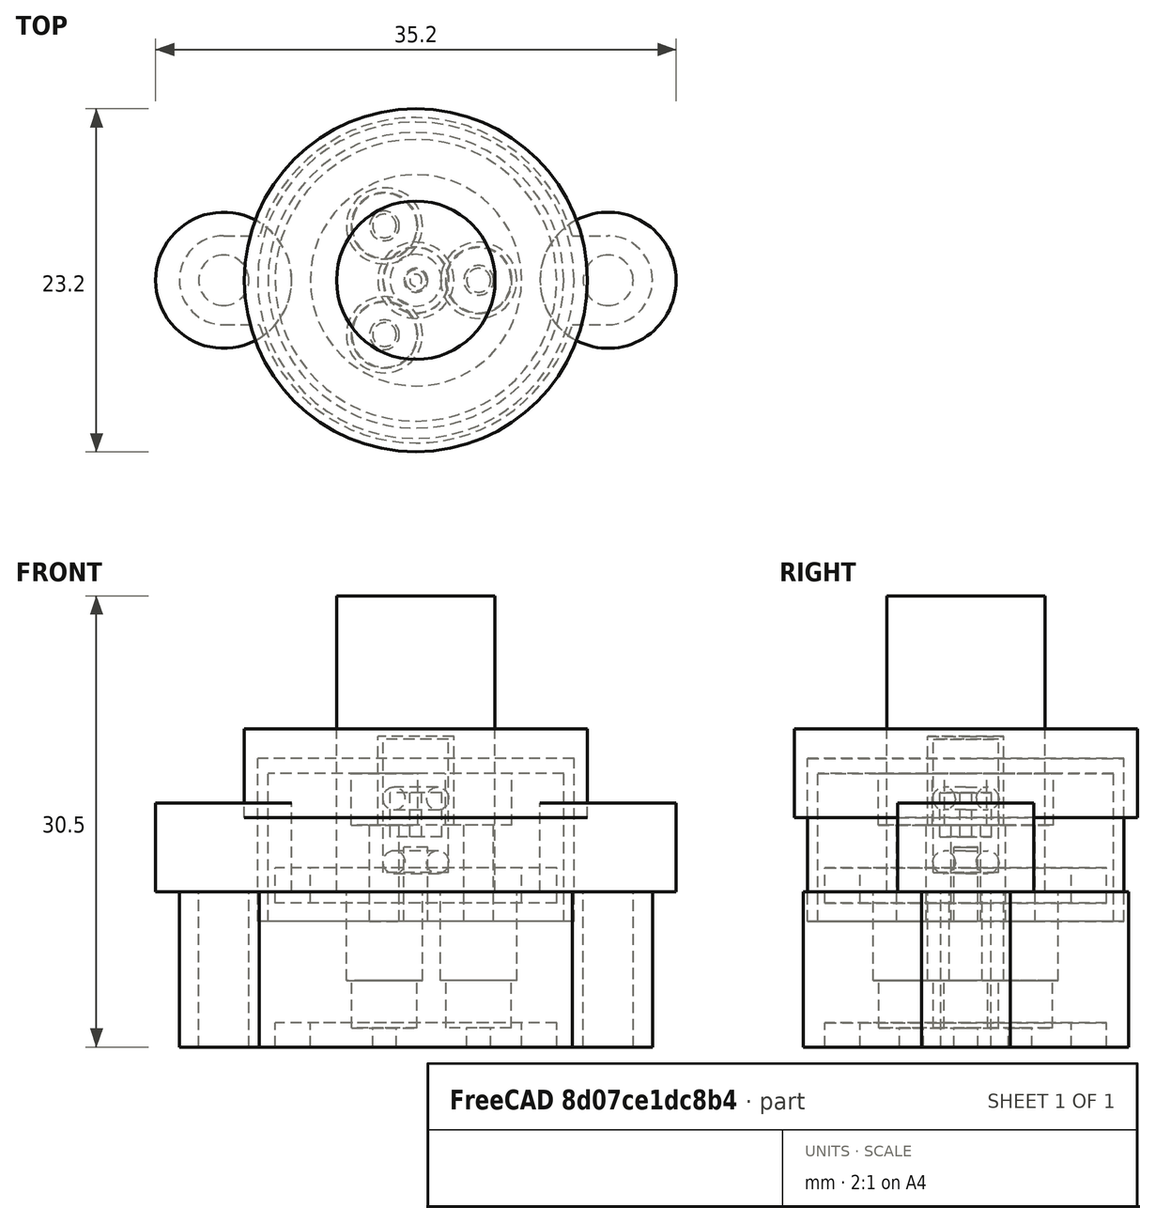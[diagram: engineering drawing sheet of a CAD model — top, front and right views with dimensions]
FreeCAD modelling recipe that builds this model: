
FCSTD DOCUMENT  (FreeCAD 0.17R13509 (Git))
Label: ceramic_wire_feedthroughs_insert_tail_negative
License: All rights reserved
LicenseURL: http://en.wikipedia.org/wiki/All_rights_reserved
objects: Part::Cylinder×46, Part::Cut×10, Part::MultiFuse×10, Part::Box×6, Part::FeaturePython×4, Part::Feature×2, App::FeaturePython×1
note: 78 computed .brp shape members not serialized (recipe doc carries the construction recipe); baked Part::Feature solids carry a one-line shape summary decoded from their .brp

FEATURE [Part::Cylinder] Cylinder155  label="Cylinder009"
  Angle = 360
  AttacherType = Attacher::AttachEngine3D
  Height = 2.38125
  Radius = 9.525
  expr: Radius = 3 / 4 * 25.399999999999999 / 2
  expr: Height = 3 / 32 * 25.399999999999999
FEATURE [Part::Cylinder] Cylinder154  label="Cylinder008"
  Angle = 360
  AttacherType = Attacher::AttachEngine3D
  Height = 2.38125
  Radius = 7.14375
  expr: Radius = 9 / 16 * 25.399999999999999 / 2
  expr: Height = 3 / 32 * 25.399999999999999
FEATURE [Part::Feature] Part__Feature001  label="TopOring"
  Placement = pos=(0,0,6.3) rot=(0,0,1;0rad)
  shape: bbox 4.839 x 4.839 x 1.524 mm, 4 faces (baked)
FEATURE [Part::Feature] Part__Feature002  label="BottomOring"
  Placement = pos=(0,0,2) rot=(0,0,1;0rad)
  shape: bbox 4.839 x 4.839 x 1.524 mm, 4 faces (baked)
FEATURE [Part::Cylinder] Cylinder153  label="Body"
  Angle = 360
  AttacherType = Attacher::AttachEngine3D
  Height = 10
  Placement = pos=(0,0,-2) rot=(0,0,1;0rad)
  Radius = 10
FEATURE [Part::Cut] Cut019  label="Oring"
  Base = -> Cylinder155
  Placement = pos=(0,0,-0.75) rot=(0,0,1;0rad)
  Tool = -> Cylinder154
FEATURE [Part::Cylinder] Cylinder147  label="ThreadedSection"
  Angle = 360
  AttacherType = Attacher::AttachEngine3D
  Height = 1
  Placement = pos=(0,0,4.5) rot=(0,0,1;0rad)
  Radius = 1
FEATURE [Part::Cylinder] Cylinder149  label="FTBead"
  Angle = 360
  AttacherType = Attacher::AttachEngine3D
  Height = 3
  Placement = pos=(0,0,2.7) rot=(0,0,1;0rad)
  Radius = 1.75
  expr: Radius = 3.5 / 2
FEATURE [Part::Cylinder] Cylinder152  label="RFFeeds005"
  Angle = 360
  AttacherType = Attacher::AttachEngine3D
  Height = 20
  Radius = 5.35813
  expr: Placement.Base.x = 0
FEATURE [Part::Cylinder] Cylinder156  label="BottomWireOutlet"
  Angle = 360
  AttacherType = Attacher::AttachEngine3D
  Height = 14
  Placement = pos=(0,0,-7) rot=(0,0,1;0rad)
  Radius = 1
FEATURE [Part::Cylinder] Cylinder157  label="SealSubtraction"
  Angle = 360
  AttacherType = Attacher::AttachEngine3D
  Height = 7
  Placement = pos=(0,0,4.5) rot=(0,0,1;0rad)
  Radius = 2.25
FEATURE [Part::MultiFuse] Fusion
  Placement = pos=(4.25,0,0) rot=(0,0,1;0rad)
  Shapes = -> [Cylinder147,Cylinder157,Cylinder156]
FEATURE [Part::FeaturePython] Array  label="SealArray"  # Draft array (typed FeaturePython)
  Angle = 360
  ArrayType = 1
  Axis = (0,0,1)
  Base = -> Fusion
  Center = (0,0,0)
  Fuse = false
  IntervalAxis = (0,0,0)
  IntervalX = (1,0,0)
  IntervalY = (0,1,0)
  IntervalZ = (0,0,0)
  NumberPolar = 3
  NumberX = 2
  NumberY = 2
  NumberZ = 1
FEATURE [Part::Cylinder] Cylinder159  label="FTBeadHole"
  Angle = 360
  AttacherType = Attacher::AttachEngine3D
  Height = 17
  Radius = 0.405
  expr: Radius = 0.81000000000000005 / 2
FEATURE [Part::Cut] Cut020
  Base = -> Cylinder149
  Placement = pos=(0,0,1) rot=(0,0,1;0rad)
  Tool = -> Cylinder159
FEATURE [Part::Cylinder] Cylinder160  label="Cylinder010"
  Angle = 360
  AttacherType = Attacher::AttachEngine3D
  Height = 2.38125
  Radius = 9.525
  expr: Radius = 3 / 4 * 25.399999999999999 / 2
  expr: Height = 3 / 32 * 25.399999999999999
FEATURE [Part::Cylinder] Cylinder161  label="WireFeedsMount003"
  Angle = 360
  AttacherType = Attacher::AttachEngine3D
  Height = 11
  Placement = pos=(-13,0,0) rot=(0,0,1;0rad)
  Radius = 1.7
FEATURE [Part::Cylinder] Cylinder162  label="ThreadedSection001"
  Angle = 360
  AttacherType = Attacher::AttachEngine3D
  Height = 6
  Placement = pos=(0,0,4.5) rot=(0,0,1;0rad)
  Radius = 2.575
  expr: Radius = 5.1500000000000004 / 2
FEATURE [Part::Cylinder] Cylinder163  label="Cylinder011"
  Angle = 360
  AttacherType = Attacher::AttachEngine3D
  Height = 2.38125
  Radius = 7.14375
  expr: Radius = 9 / 16 * 25.399999999999999 / 2
  expr: Height = 3 / 32 * 25.399999999999999
FEATURE [Part::Cut] Cut022  label="Oring001"
  Base = -> Cylinder160
  Placement = pos=(0,0,-0.75) rot=(0,0,1;0rad)
  Tool = -> Cylinder163
FEATURE [Part::Cylinder] Cylinder164  label="Body001"
  Angle = 360
  AttacherType = Attacher::AttachEngine3D
  Height = 10.5
  Radius = 11
FEATURE [Part::Cylinder] Cylinder165  label="WireFeedsMount004"
  Angle = 360
  AttacherType = Attacher::AttachEngine3D
  Height = 11
  Placement = pos=(13,0,0) rot=(0,0,1;0rad)
  Radius = 1.7
FEATURE [Part::Cylinder] Cylinder166  label="BottomWireOutlet001"
  Angle = 360
  AttacherType = Attacher::AttachEngine3D
  Height = 5
  Placement = pos=(0,0,-2) rot=(0,0,1;0rad)
  Radius = 0.8
FEATURE [Part::Cylinder] Cylinder167  label="SealSubtraction001"
  Angle = 360
  AttacherType = Attacher::AttachEngine3D
  Height = 9
  Placement = pos=(0,0,1.3) rot=(0,0,1;0rad)
  Radius = 2.2
FEATURE [Part::Box] Box002  label="MountCube003"
  AttacherType = Attacher::AttachEngine3D
  Height = 10.5
  Length = 3
  Placement = pos=(10,-3,0) rot=(0,0,1;0rad)
  Width = 6
FEATURE [Part::Box] Box003  label="MountCube004"
  AttacherType = Attacher::AttachEngine3D
  Height = 10.5
  Length = 3
  Placement = pos=(-13,-3,0) rot=(0,0,1;0rad)
  Width = 6
FEATURE [Part::MultiFuse] Fusion004
  Placement = pos=(4.25,0,0) rot=(0,0,1;0rad)
  Shapes = -> [Cylinder162,Cylinder167,Cylinder166]
FEATURE [Part::Cylinder] Cylinder168  label="MountFlange003"
  Angle = 360
  AttacherType = Attacher::AttachEngine3D
  Height = 10.5
  Placement = pos=(-13,0,0) rot=(0,0,1;0rad)
  Radius = 3
FEATURE [Part::Cylinder] Cylinder169  label="MountFlange004"
  Angle = 360
  AttacherType = Attacher::AttachEngine3D
  Height = 10.5
  Placement = pos=(13,0,0) rot=(0,0,1;0rad)
  Radius = 3
FEATURE [Part::MultiFuse] Fusion003
  Shapes = -> [Cylinder169,Box002,Box003,Cylinder168,Cylinder164]
FEATURE [Part::FeaturePython] Array001  label="SealArray001"  # Draft array (typed FeaturePython)
  Angle = 360
  ArrayType = 1
  Axis = (0,0,1)
  Base = -> Fusion004
  Center = (0,0,0)
  Fuse = false
  IntervalAxis = (0,0,0)
  IntervalX = (1,0,0)
  IntervalY = (0,1,0)
  IntervalZ = (0,0,0)
  NumberPolar = 3
  NumberX = 2
  NumberY = 2
  NumberZ = 1
FEATURE [Part::MultiFuse] Fusion005
  Shapes = -> [Cylinder165,Cylinder161,Cut022,Array001]
FEATURE [Part::Cut] Cut021
  Base = -> Fusion003
  Placement = pos=(0,0,-10.5) rot=(0,0,1;0rad)
  Tool = -> Fusion005
FEATURE [Part::Cylinder] Cylinder170  label="Cylinder012"
  Angle = 360
  AttacherType = Attacher::AttachEngine3D
  Height = 2.38125
  Radius = 9.525
  expr: Radius = 3 / 4 * 25.399999999999999 / 2
  expr: Height = 3 / 32 * 25.399999999999999
FEATURE [Part::Cylinder] Cylinder171  label="WireFeedsMount005"
  Angle = 360
  AttacherType = Attacher::AttachEngine3D
  Height = 11
  Placement = pos=(-13,0,0) rot=(0,0,1;0rad)
  Radius = 1.7
FEATURE [Part::Cylinder] Cylinder172  label="ThreadedSection002"
  Angle = 360
  AttacherType = Attacher::AttachEngine3D
  Height = 6
  Placement = pos=(0,0,4.5) rot=(0,0,1;0rad)
  Radius = 2.575
  expr: Radius = 5.1500000000000004 / 2
FEATURE [Part::Cylinder] Cylinder173  label="Cylinder013"
  Angle = 360
  AttacherType = Attacher::AttachEngine3D
  Height = 2.38125
  Radius = 7.14375
  expr: Radius = 9 / 16 * 25.399999999999999 / 2
  expr: Height = 3 / 32 * 25.399999999999999
FEATURE [Part::Cut] Cut024  label="Oring002"
  Base = -> Cylinder170
  Placement = pos=(0,0,-0.75) rot=(0,0,1;0rad)
  Tool = -> Cylinder173
FEATURE [Part::Cylinder] Cylinder174  label="Body002"
  Angle = 360
  AttacherType = Attacher::AttachEngine3D
  Height = 10.5
  Radius = 11
FEATURE [Part::Cylinder] Cylinder175  label="WireFeedsMount006"
  Angle = 360
  AttacherType = Attacher::AttachEngine3D
  Height = 11
  Placement = pos=(13,0,0) rot=(0,0,1;0rad)
  Radius = 1.7
FEATURE [Part::Cylinder] Cylinder176  label="BottomWireOutlet002"
  Angle = 360
  AttacherType = Attacher::AttachEngine3D
  Height = 5
  Placement = pos=(0,0,-2) rot=(0,0,1;0rad)
  Radius = 0.8
FEATURE [Part::Cylinder] Cylinder177  label="SealSubtraction002"
  Angle = 360
  AttacherType = Attacher::AttachEngine3D
  Height = 9
  Placement = pos=(0,0,1.3) rot=(0,0,1;0rad)
  Radius = 2.2
FEATURE [Part::Box] Box004  label="MountCube005"
  AttacherType = Attacher::AttachEngine3D
  Height = 10.5
  Length = 3
  Placement = pos=(10,-3,0) rot=(0,0,1;0rad)
  Width = 6
FEATURE [App::FeaturePython] SetupSheet002  # Path/CAM operation (typed FeaturePython)
  ClearanceHeightExpression = StartDepth+SetupSheet.ClearanceHeightOffset
  ClearanceHeightOffset = 5
  FinalDepthExpression = OpFinalDepth
  HorizRapid = 0
  SafeHeightExpression = StartDepth+SetupSheet.SafeHeightOffset
  SafeHeightOffset = 3
  StartDepthExpression = OpStartDepth
  StepDownExpression = OpToolDiameter
  VertRapid = 0
FEATURE [Part::Box] Box005  label="MountCube006"
  AttacherType = Attacher::AttachEngine3D
  Height = 10.5
  Length = 3
  Placement = pos=(-13,-3,0) rot=(0,0,1;0rad)
  Width = 6
FEATURE [Part::MultiFuse] Fusion007
  Placement = pos=(4.25,0,0) rot=(0,0,1;0rad)
  Shapes = -> [Cylinder172,Cylinder177,Cylinder176]
FEATURE [Part::Cylinder] Cylinder178  label="MountFlange005"
  Angle = 360
  AttacherType = Attacher::AttachEngine3D
  Height = 10.5
  Placement = pos=(-13,0,0) rot=(0,0,1;0rad)
  Radius = 3
FEATURE [Part::Cylinder] Cylinder179  label="MountFlange006"
  Angle = 360
  AttacherType = Attacher::AttachEngine3D
  Height = 10.5
  Placement = pos=(13,0,0) rot=(0,0,1;0rad)
  Radius = 3
FEATURE [Part::MultiFuse] Fusion006
  Shapes = -> [Cylinder179,Box004,Box005,Cylinder178,Cylinder174]
FEATURE [Part::FeaturePython] Array002  label="SealArray002"  # Draft array (typed FeaturePython)
  Angle = 360
  ArrayType = 1
  Axis = (0,0,1)
  Base = -> Fusion007
  Center = (0,0,0)
  Fuse = false
  IntervalAxis = (0,0,0)
  IntervalX = (1,0,0)
  IntervalY = (0,1,0)
  IntervalZ = (0,0,0)
  NumberPolar = 3
  NumberX = 2
  NumberY = 2
  NumberZ = 1
FEATURE [Part::MultiFuse] Fusion008
  Shapes = -> [Cylinder175,Cylinder171,Cut024,Array002]
FEATURE [Part::Cut] Cut023
  Base = -> Fusion006
  Placement = pos=(0,0,-10.5) rot=(0,0,1;0rad)
  Tool = -> Fusion008
FEATURE [Part::Cylinder] Cylinder180  label="Cylinder014"
  Angle = 360
  AttacherType = Attacher::AttachEngine3D
  Height = 2.38125
  Radius = 7.14375
  expr: Radius = 9 / 16 * 25.399999999999999 / 2
  expr: Height = 3 / 32 * 25.399999999999999
FEATURE [Part::Cylinder] Cylinder181  label="MountFlange007"
  Angle = 360
  AttacherType = Attacher::AttachEngine3D
  Height = 10.5
  Placement = pos=(-13,0,0) rot=(0,0,1;0rad)
  Radius = 3
FEATURE [Part::Box] Box006  label="MountCube007"
  AttacherType = Attacher::AttachEngine3D
  Height = 10.5
  Length = 3
  Placement = pos=(-13,-3,0) rot=(0,0,1;0rad)
  Width = 6
FEATURE [Part::Cylinder] Cylinder182  label="WireFeedsMount007"
  Angle = 360
  AttacherType = Attacher::AttachEngine3D
  Height = 11
  Placement = pos=(13,0,0) rot=(0,0,1;0rad)
  Radius = 1.7
FEATURE [Part::Box] Box007  label="MountCube008"
  AttacherType = Attacher::AttachEngine3D
  Height = 10.5
  Length = 3
  Placement = pos=(10,-3,0) rot=(0,0,1;0rad)
  Width = 6
FEATURE [Part::Cylinder] Cylinder183  label="WireFeedsMount008"
  Angle = 360
  AttacherType = Attacher::AttachEngine3D
  Height = 11
  Placement = pos=(-13,0,0) rot=(0,0,1;0rad)
  Radius = 1.7
FEATURE [Part::Cylinder] Cylinder184  label="Body003"
  Angle = 360
  AttacherType = Attacher::AttachEngine3D
  Height = 10.5
  Radius = 11
FEATURE [Part::Cylinder] Cylinder185  label="MountFlange008"
  Angle = 360
  AttacherType = Attacher::AttachEngine3D
  Height = 10.5
  Placement = pos=(13,0,0) rot=(0,0,1;0rad)
  Radius = 3
FEATURE [Part::Cylinder] Cylinder186  label="BottomWireOutlet003"
  Angle = 360
  AttacherType = Attacher::AttachEngine3D
  Height = 5
  Placement = pos=(0,0,-2) rot=(0,0,1;0rad)
  Radius = 0.8
FEATURE [Part::MultiFuse] Fusion011
  Shapes = -> [Cylinder185,Box007,Box006,Cylinder181,Cylinder184]
FEATURE [Part::Cylinder] Cylinder187  label="ThreadedSection003"
  Angle = 360
  AttacherType = Attacher::AttachEngine3D
  Height = 6
  Placement = pos=(0,0,4.5) rot=(0,0,1;0rad)
  Radius = 2.575
  expr: Radius = 5.1500000000000004 / 2
FEATURE [Part::Cylinder] Cylinder188  label="Cylinder015"
  Angle = 360
  AttacherType = Attacher::AttachEngine3D
  Height = 2.38125
  Radius = 9.525
  expr: Radius = 3 / 4 * 25.399999999999999 / 2
  expr: Height = 3 / 32 * 25.399999999999999
FEATURE [Part::Cut] Cut025  label="Oring003"
  Base = -> Cylinder188
  Placement = pos=(0,0,-0.75) rot=(0,0,1;0rad)
  Tool = -> Cylinder180
FEATURE [Part::Cylinder] Cylinder189  label="SealSubtraction003"
  Angle = 360
  AttacherType = Attacher::AttachEngine3D
  Height = 9
  Placement = pos=(0,0,1.3) rot=(0,0,1;0rad)
  Radius = 2.2
FEATURE [Part::MultiFuse] Fusion009
  Placement = pos=(4.25,0,0) rot=(0,0,1;0rad)
  Shapes = -> [Cylinder187,Cylinder189,Cylinder186]
FEATURE [Part::FeaturePython] Array003  label="SealArray003"  # Draft array (typed FeaturePython)
  Angle = 360
  ArrayType = 1
  Axis = (0,0,1)
  Base = -> Fusion009
  Center = (0,0,0)
  Fuse = false
  IntervalAxis = (0,0,0)
  IntervalX = (1,0,0)
  IntervalY = (0,1,0)
  IntervalZ = (0,0,0)
  NumberPolar = 3
  NumberX = 2
  NumberY = 2
  NumberZ = 1
FEATURE [Part::MultiFuse] Fusion010
  Shapes = -> [Cylinder182,Cylinder183,Cut025,Array003]
FEATURE [Part::Cut] Cut026
  Base = -> Fusion011
  Placement = pos=(0,0,-10.5) rot=(0,0,1;0rad)
  Tool = -> Fusion010
FEATURE [Part::Cylinder] Cylinder192  label="ThreadedSection004"
  Angle = 360
  AttacherType = Attacher::AttachEngine3D
  Height = 6
  Placement = pos=(0,0,4.5) rot=(0,0,1;0rad)
  Radius = 2.575
  expr: Radius = 5.1500000000000004 / 2
FEATURE [Part::Cylinder] Cylinder196  label="BottomWireOutlet004"
  Angle = 360
  AttacherType = Attacher::AttachEngine3D
  Height = 5
  Placement = pos=(0,0,-2) rot=(0,0,1;0rad)
  Radius = 0.8
FEATURE [Part::Cylinder] Cylinder197  label="SealSubtraction004"
  Angle = 360
  AttacherType = Attacher::AttachEngine3D
  Height = 9
  Placement = pos=(0,0,1.3) rot=(0,0,1;0rad)
  Radius = 2.2
FEATURE [Part::Cylinder] Cylinder198  label="Cylinder"
  Angle = 360
  AttacherType = Attacher::AttachEngine3D
  Height = 6
  Placement = pos=(0,0,5) rot=(0,0,1;0rad)
  Radius = 11.6
FEATURE [Part::Cylinder] Cylinder199  label="Cylinder016"
  Angle = 360
  AttacherType = Attacher::AttachEngine3D
  Height = 6
  Placement = pos=(-13,0,0) rot=(0,0,1;0rad)
  Radius = 4.6
FEATURE [Part::Cylinder] Cylinder200  label="Cylinder017"
  Angle = 360
  AttacherType = Attacher::AttachEngine3D
  Height = 6
  Placement = pos=(13,0,0) rot=(0,0,1;0rad)
  Radius = 4.6
FEATURE [Part::Cut] Cut
  Base = -> Cylinder153
  Tool = -> Array
FEATURE [Part::Cylinder] Cylinder  label="Cylinder018"
  Angle = 360
  AttacherType = Attacher::AttachEngine3D
  Height = 11
  Placement = pos=(0,0,-2) rot=(0,0,1;0rad)
  Radius = 10.7
FEATURE [Part::Cut] Cut027
  Base = -> Cylinder
  Tool = -> Cut
